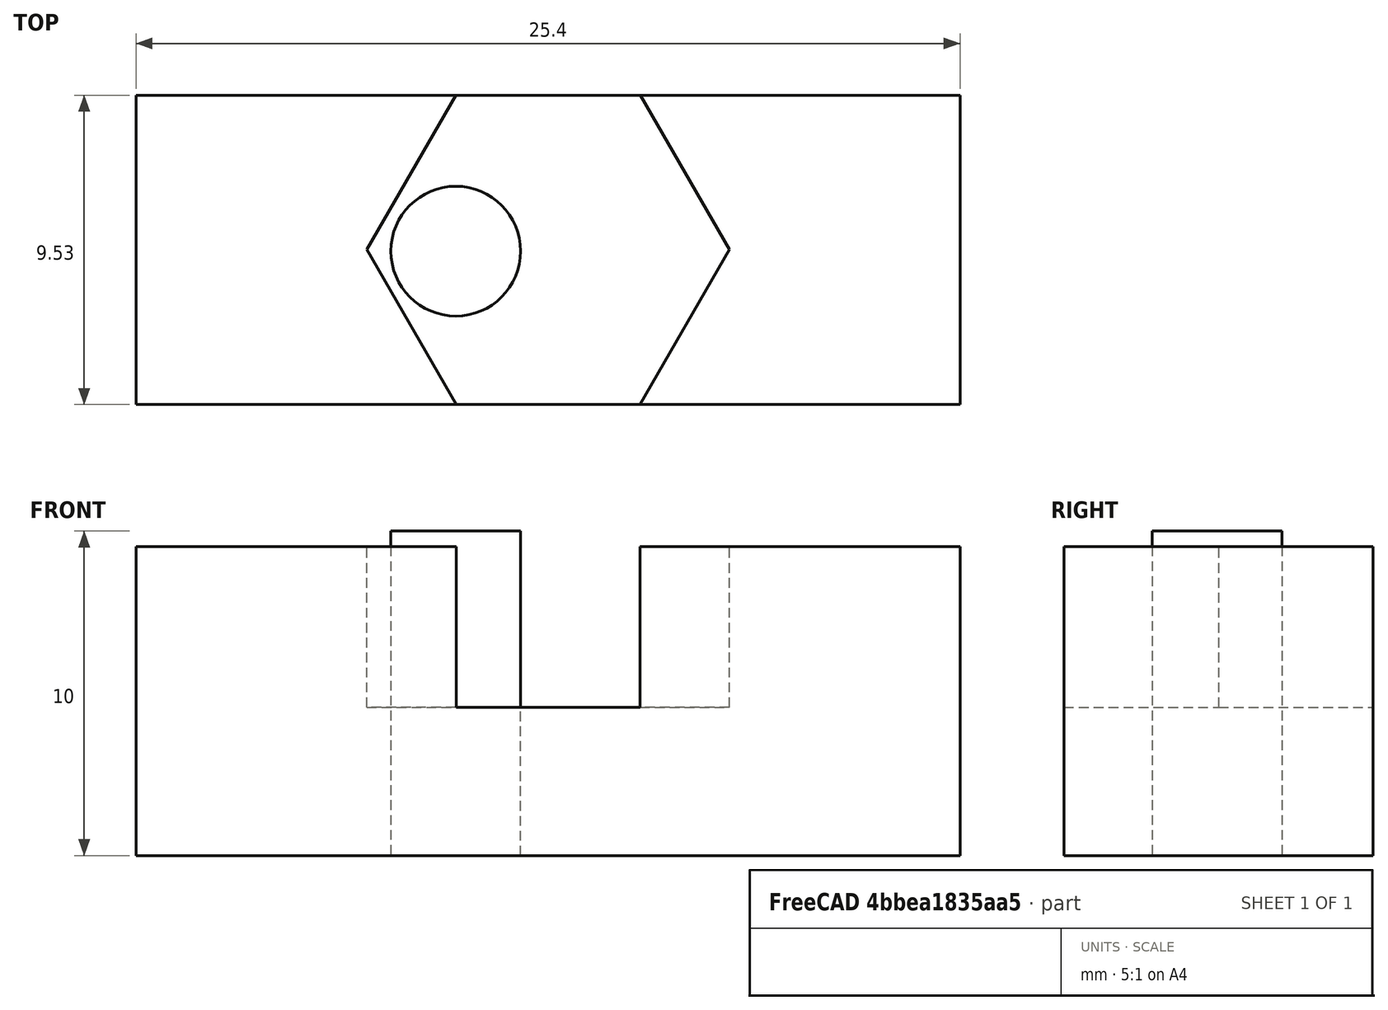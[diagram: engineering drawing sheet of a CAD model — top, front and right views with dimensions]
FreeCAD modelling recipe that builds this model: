
FCSTD DOCUMENT  (FreeCAD 0.21R33771 (Git))
Label: nutholder
License: All rights reserved
LicenseURL: http://en.wikipedia.org/wiki/All_rights_reserved
objects: Part::RegularPolygon×1, Part::Extrusion×1, Part::Box×1, Part::Cut×1, Part::Cylinder×1
note: 5 computed .brp shape members not serialized (recipe doc carries the construction recipe); baked Part::Feature solids carry a one-line shape summary decoded from their .brp

FEATURE [Part::RegularPolygon] RegularPolygon  label="Regular polygon"
  AttacherType = Attacher::AttachEngine3D
  Circumradius = 5.588
  Polygon = 6
FEATURE [Part::Extrusion] Extrude
  Base = -> RegularPolygon
  Dir = (0,0,1)
  DirMode = 2
  FaceMakerClass = Part::FaceMakerBullseye
  LengthFwd = 5.08
  LengthRev = 0
  Placement = pos=(12.7,4.7752,4.572) rot=(0,0,1;0rad)
  Solid = true
  Symmetric = false
FEATURE [Part::Box] Box  label="Cube"
  AttacherType = Attacher::AttachEngine3D
  Height = 9.525
  Length = 25.4
  Width = 9.525
FEATURE [Part::Cut] Cut
  Base = -> Box
  Tool = -> Extrude
FEATURE [Part::Cylinder] Cylinder
  Angle = 360
  AttacherType = Attacher::AttachEngine3D
  FirstAngle = 0
  Height = 10
  Placement = pos=(9.8552,4.7244,0) rot=(0,0,1;0rad)
  Radius = 2
  SecondAngle = 0
